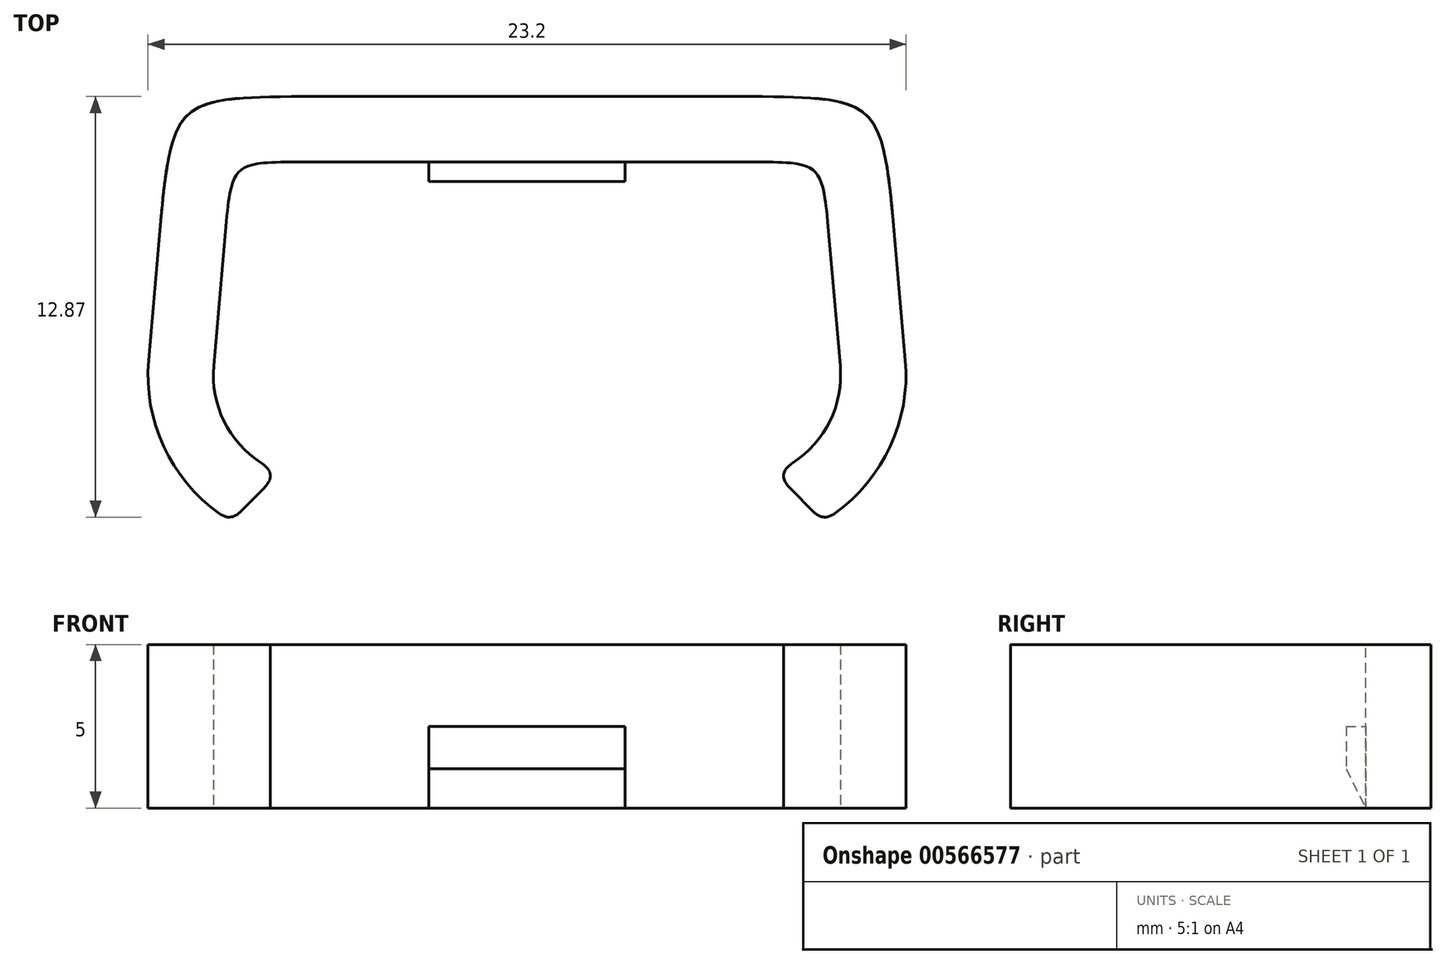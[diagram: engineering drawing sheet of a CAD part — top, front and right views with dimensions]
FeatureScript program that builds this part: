
annotation { "Feature Type Name" : "Feature", "Feature Type Description" : "" }
export const myFeature = defineFeature(function(context is Context, id is Id, definition is map)
    precondition{}
    {
        {
            var Q0;
            Q0=qCreatedBy(makeId("Top.planeOp"),FACE);
            var sketch = newSketch(context, id + "F0", { "sketchPlane" : qUnion([Q0])});
            skLineSegment(sketch, "E0", {"start": v(0, 0) * mm, "end": v(7.15, 0) * mm});
            skLineSegment(sketch, "E1", {"start": v(7.15, 0) * mm, "end": v(7.15, -3) * mm});
            skArc(sketch, "E2", {"start": v(8.15, -9.67) * mm, "mid": v(9.96, -5.99) * mm, "end": v(7.15, -3) * mm});
            skLineSegment(sketch, "E3", {"start": v(7.15, -3) * mm, "end": v(0, -3) * mm, "construction": true});
            skLineSegment(sketch, "E4", {"start": v(10, -6.52) * mm, "end": v(10, 0) * mm, "construction": true});
            skLineSegment(sketch, "E5", {"start": v(10, 0) * mm, "end": v(7.15, 0) * mm, "construction": true});
            skSolve(sketch);
        }
        {
            var Q0;
            Q0=qCreatedBy(makeId("Top.planeOp"),FACE);
            var sketch = newSketch(context, id + "F1", { "sketchPlane" : qUnion([Q0])});
            skArc(sketch, "E6", {"start": v(-54.7, 8.13) * mm, "mid": v(0, -13.5) * mm, "end": v(54.7, 8.13) * mm});
            skLineSegment(sketch, "E7", {"start": v(0, 66.5) * mm, "end": v(0, 0) * mm, "construction": true});
            skLineSegment(sketch, "E8", {"start": v(0, 0) * mm, "end": v(0, -13.5) * mm, "construction": true});
            skArc(sketch, "E9", {"start": v(-43.93, 4.75) * mm, "mid": v(0, -13.5) * mm, "end": v(43.93, 4.75) * mm, "construction": true});
            skSolve(sketch);
        }
        {
            var Q0;
            Q0=qCreatedBy(makeId("Top.planeOp"),FACE);
            var sketch = newSketch(context, id + "F2", { "sketchPlane" : qUnion([Q0])});
            skLineSegment(sketch, "E10", {"start": v(0, 0) * mm, "end": v(0, 2) * mm});
            skLineSegment(sketch, "E11", {"start": v(0, 2) * mm, "end": v(10.87, 2) * mm});
            skLineSegment(sketch, "E12", {"start": v(9.06, -10.99) * mm, "end": v(7.57, -9.5) * mm});
            skLineSegment(sketch, "E13", {"start": v(0, 0) * mm, "end": v(9.04, 0) * mm});
            skLineSegment(sketch, "E14", {"start": v(9.04, 0) * mm, "end": v(9.59, -6.24) * mm});
            skArc(sketch, "E15", {"start": v(7.57, -9.5) * mm, "mid": v(9.12, -8.2) * mm, "end": v(9.59, -6.24) * mm});
            skLineSegment(sketch, "E16", {"start": v(10.87, 2) * mm, "end": v(11.58, -6.07) * mm});
            skArc(sketch, "E17", {"start": v(9.06, -10.99) * mm, "mid": v(11.03, -8.9) * mm, "end": v(11.58, -6.07) * mm});
            skSolve(sketch);
        }
        {
            var Q0;
            Q0=qSketchRegion(id+"F2",true);
            extrude(context, id + "F3", {"entities" : qUnion([Q0]), "depth" : 5 * mm});
        }
        {
            var Q0;
            Q0=makeQuery(id+"F3.opExtrude","SWEPT_EDGE",EDGE,{"disambiguationData":[OSD([sQuery(id+"F2.wireOp",EDGE,"E13"),sQuery(id+"F2.wireOp",EDGE,"E14")])]});
            fillet(context, id + "F4", {"entities" : qUnion([Q0]), "radius" : 2 * mm, "tangentPropagation" : true, "rho" : .7, "crossSection" : FilletCrossSection.CONIC, "allowEdgeOverflow" : false});
        }
        {
            var Q0;
            Q0=makeQuery(id+"F3.opExtrude","SWEPT_EDGE",EDGE,{"disambiguationData":[OSD([sQuery(id+"F2.wireOp",EDGE,"E11"),sQuery(id+"F2.wireOp",EDGE,"E16")])]});
            fillet(context, id + "F5", {"entities" : qUnion([Q0]), "radius" : 4 * mm, "tangentPropagation" : true, "rho" : .7, "crossSection" : FilletCrossSection.CONIC, "allowEdgeOverflow" : false});
        }
        {
            var Q0;
            Q0=makeQuery(id+"F3.opExtrude","SWEPT_FACE",FACE,{"disambiguationData":[OSD([sQuery(id+"F2.wireOp",EDGE,"E13")])]});
            var sketch = newSketch(context, id + "F6", { "sketchPlane" : qUnion([Q0])});
            skLineSegment(sketch, "E18.bottom", {"start": v(0, 2.5) * mm, "end": v(3, 2.5) * mm});
            skLineSegment(sketch, "E18.top", {"start": v(0, 0) * mm, "end": v(3, 0) * mm});
            skLineSegment(sketch, "E18.left", {"start": v(0, 2.5) * mm, "end": v(0, 0) * mm});
            skLineSegment(sketch, "E18.right", {"start": v(3, 2.5) * mm, "end": v(3, 0) * mm});
            skSolve(sketch);
        }
        {
            var Q0;
            Q0=qSketchRegion(id+"F6",true);
            extrude(context, id + "F7", {"entities" : qUnion([Q0]), "operationType" : NewBodyOperationType.ADD, "depth" : 0.6 * mm});
        }
        {
            var Q0;
            Q0=makeQuery(id+"F7.opExtrude","CAP_EDGE",EDGE,{"disambiguationData":[OSD([sQuery(id+"F6.wireOp",EDGE,"E18.top")])],"isStart":false});
            chamfer(context, id + "F8", {"entities" : qUnion([Q0]), "chamferType" : ChamferType.TWO_OFFSETS, "width1" : 1.2 * mm, "oppositeDirection" : false, "width2" : .6 * mm, "tangentPropagation" : true});
        }
        {
            var Q0;
            Q0=qCreatedBy(makeId("Top.planeOp"),FACE);
            var sketch = newSketch(context, id + "F9", { "sketchPlane" : qUnion([Q0])});
            skArc(sketch, "E19", {"start": v(9.06, -10.99) * mm, "mid": v(11.06, -12.2) * mm, "end": v(13.4, -12.37) * mm});
            skArc(sketch, "E20", {"start": v(13.4, -12.37) * mm, "mid": v(15.74, -11.94) * mm, "end": v(18.07, -11.43) * mm});
            skLineSegment(sketch, "E21", {"start": v(18.07, -11.43) * mm, "end": v(18.26, -10.36) * mm});
            skArc(sketch, "E22", {"start": v(13.22, -11.39) * mm, "mid": v(15.75, -10.91) * mm, "end": v(18.26, -10.36) * mm});
            skArc(sketch, "E23", {"start": v(9.88, -10.39) * mm, "mid": v(11.43, -11.28) * mm, "end": v(13.22, -11.39) * mm});
            skLineSegment(sketch, "E24", {"start": v(9.88, -10.39) * mm, "end": v(9.06, -10.99) * mm});
            skSolve(sketch);
        }
        {
            var Q0;
            Q0=makeQuery(id+"F3.opExtrude","SWEPT_EDGE",EDGE,{"disambiguationData":[OSD([sQuery(id+"F2.wireOp",EDGE,"E12"),sQuery(id+"F2.wireOp",EDGE,"E15")])]});
            var Q1;
            Q1=makeQuery(id+"F3.opExtrude","SWEPT_EDGE",EDGE,{"disambiguationData":[OSD([sQuery(id+"F2.wireOp",EDGE,"E12"),sQuery(id+"F2.wireOp",EDGE,"E17")])]});
            fillet(context, id + "F10", {"entities" : qUnion([Q0, Q1]), "radius" : .5 * mm, "tangentPropagation" : true, "rho" : .5, "crossSection" : FilletCrossSection.CONIC, "allowEdgeOverflow" : false});
        }
        {
            var Q0;
            Q0=makeQuery(id+"F3.opExtrude","SWEPT_BODY",BODY,{"disambiguationData":[OSD([sQuery(id+"F2.wireOp",EDGE,"E10"),sQuery(id+"F2.wireOp",EDGE,"E11"),sQuery(id+"F2.wireOp",EDGE,"E12"),sQuery(id+"F2.wireOp",EDGE,"E13"),sQuery(id+"F2.wireOp",EDGE,"E14"),sQuery(id+"F2.wireOp",EDGE,"E15"),sQuery(id+"F2.wireOp",EDGE,"E16"),sQuery(id+"F2.wireOp",EDGE,"E17")])]});
            var Q1;
            Q1=makeQuery(id+"F7.boolean.opBoolean","MERGE",FACE,{"derivedFrom":[makeQuery(id+"F3.opExtrude","SWEPT_FACE",FACE,{"disambiguationData":[OSD([sQuery(id+"F2.wireOp",EDGE,"E10")])]}),makeQuery(id+"F7.opExtrude","SWEPT_FACE",FACE,{"disambiguationData":[OSD([sQuery(id+"F6.wireOp",EDGE,"E18.left")])]})]});
            mirror(context, id + "F11", {"operationType" : NewBodyOperationType.ADD, "entities" : qUnion([Q0]), "mirrorPlane" : qUnion([Q1])});
        }
    });
